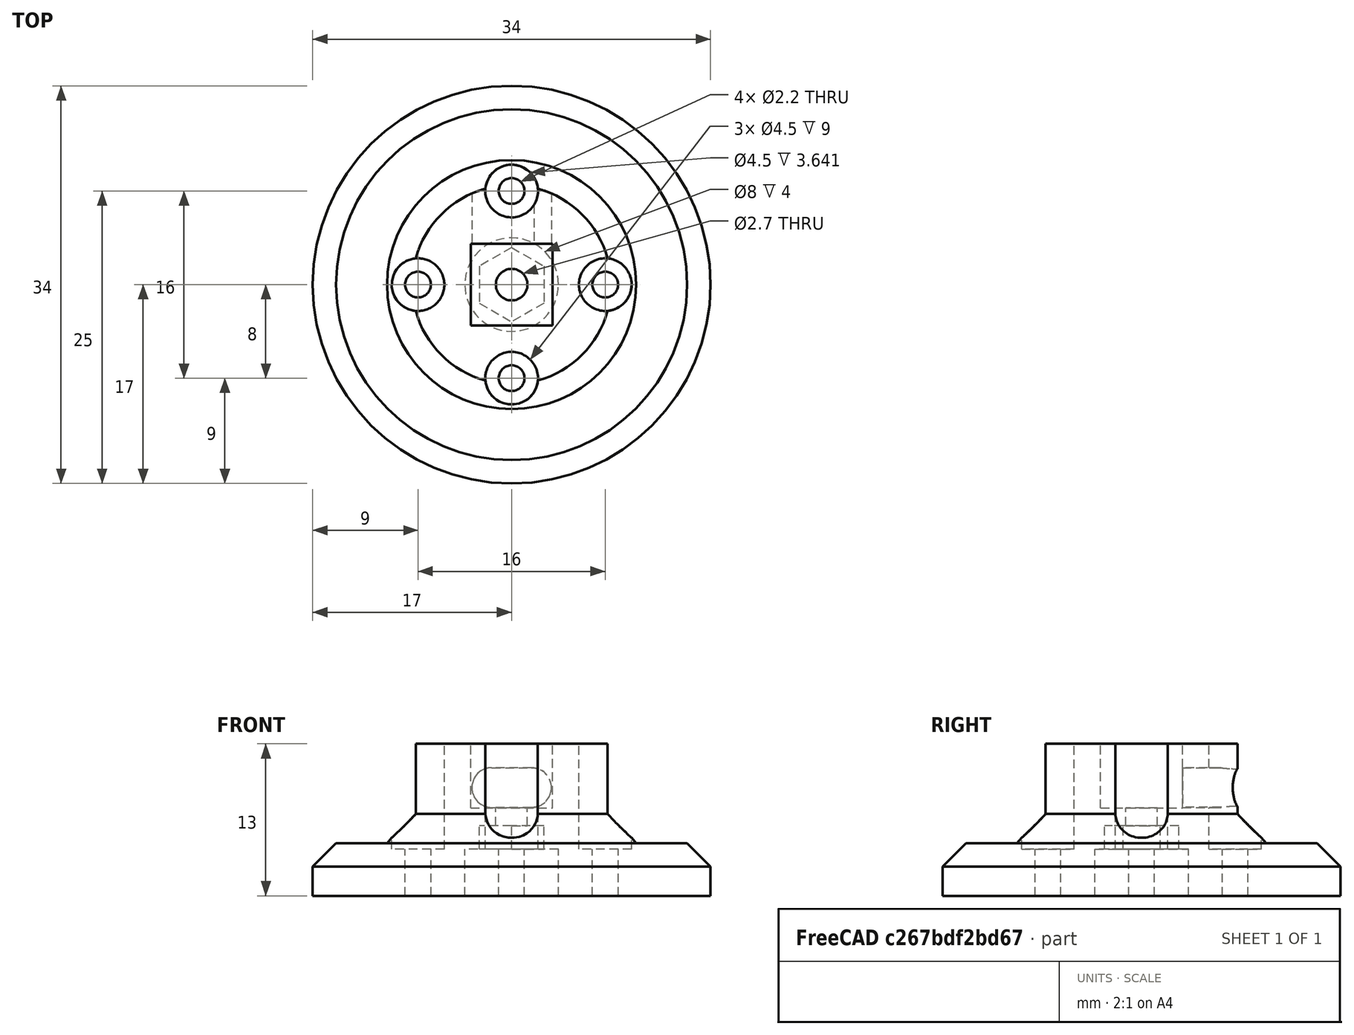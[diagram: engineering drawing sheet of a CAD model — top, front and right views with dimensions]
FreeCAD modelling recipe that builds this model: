
FCSTD DOCUMENT  (FreeCAD 0.14R2935 (Git))
Label: tendon_wheel_ax_9_17_mm
License: CC-BY 3.0
LicenseURL: http://creativecommons.org/licenses/by/3.0/
objects: Part::Cylinder×14, Part::MultiFuse×6, Part::Box×2, Part::Cone×1, Part::Extrusion×1, Part::Mirroring×1, Part::Cut×1, Part::Chamfer×1
note: 27 computed .brp shape members not serialized (recipe doc carries the construction recipe); baked Part::Feature solids carry a one-line shape summary decoded from their .brp

FEATURE [Part::Cylinder] Cylinder
  Angle = 360
  Height = 4.5
  Placement = pos=(0,0,0.5) rot=(0,0,1;0rad)
  Radius = 17
FEATURE [Part::Cone] Cone
  Angle = 360
  Height = 3.5
  Placement = pos=(0,0,4) rot=(0,0,1;0rad)
  Radius1 = 11.5
  Radius2 = 8.5
FEATURE [Part::Cylinder] Cylinder001
  Angle = 360
  Height = 6.5
  Placement = pos=(0,0,7) rot=(0,0,1;0rad)
  Radius = 8.5
FEATURE [Part::Cylinder] Cylinder003  label="TopHole003"
  Angle = 360
  Height = 20
  Placement = pos=(-8,0,-3) rot=(0,0,1;0rad)
  Radius = 1.1
FEATURE [Part::Cylinder] Cylinder004  label="TopHole002"
  Angle = 360
  Height = 20
  Placement = pos=(0,-8,-3) rot=(0,0,1;0rad)
  Radius = 1.1
FEATURE [Part::Cylinder] Cylinder005  label="TopHole001"
  Angle = 360
  Height = 20
  Placement = pos=(8,0,-3) rot=(0,0,1;0rad)
  Radius = 1.1
FEATURE [Part::Cylinder] Cylinder006  label="TopHole"
  Angle = 360
  Height = 10
  Placement = pos=(0,8,-3) rot=(0,0,1;0rad)
  Radius = 1.1
FEATURE [Part::Cylinder] Cylinder007  label="TopHole004"
  Angle = 360
  Height = 20
  Placement = pos=(-8,0,3.5) rot=(0,0,1;0rad)
  Radius = 2.25
FEATURE [Part::Cylinder] Cylinder008  label="TopHole005"
  Angle = 360
  Height = 20
  Placement = pos=(8,0,3.5) rot=(0,0,1;0rad)
  Radius = 2.25
FEATURE [Part::Cylinder] Cylinder009  label="TopHole006"
  Angle = 360
  Height = 20
  Placement = pos=(0,8,3.5) rot=(0,0,1;0rad)
  Radius = 2.25
FEATURE [Part::Cylinder] Cylinder010  label="TopHole007"
  Angle = 360
  Height = 20
  Placement = pos=(0,-8,3.5) rot=(0,0,1;0rad)
  Radius = 2.25
FEATURE [Part::MultiFuse] Fusion001
  Placement = pos=(0,0,1) rot=(0,0,1;0rad)
  Shapes = -> [Cylinder010,Cylinder007,Cylinder005,Cylinder003,Cylinder009,Cylinder004,Cylinder008,Cylinder006]
FEATURE [Part::Cylinder] Cylinder012  label="Cylinder003"
  Angle = 360
  Height = 10
  Placement = pos=(-1.7,12,9.75) rot=(1,0,0;1.5708rad)
  Radius = 1.7
FEATURE [Part::Cylinder] Cylinder013  label="Cylinder004"
  Angle = 360
  Height = 20
  Placement = pos=(0,0,-5) rot=(0,0,1;0rad)
  Radius = 1.35
FEATURE [Part::Box] Box  label="Cube"
  Height = 8
  Length = 7
  Placement = pos=(-3.5,-3.5,8) rot=(0,0,1;0rad)
  Width = 7
FEATURE [Part::Extrusion] Extrude
  Dir = (0,0,2)
  Solid = true
FEATURE [Part::Mirroring] Part__Mirroring  label="Extrude (Mirror #1)"
  Base = (0,0,0)
  Normal = (1,0,0)
  Source = -> Extrude
FEATURE [Part::MultiFuse] Fusion002
  Placement = pos=(0,0,4.5) rot=(0,0,1;0rad)
  Shapes = -> [Part__Mirroring,Extrude]
FEATURE [Part::Cylinder] Cylinder014  label="Cylinder005"
  Angle = 360
  Height = 4.5
  Radius = 4
FEATURE [Part::Cylinder] Cylinder015  label="Cylinder006"
  Angle = 360
  Height = 10
  Placement = pos=(1.7,12,9.75) rot=(1,0,0;1.5708rad)
  Radius = 1.7
FEATURE [Part::Box] Box001  label="Cube001"
  Height = 3.4
  Length = 3.6
  Placement = pos=(-1.7,2,8.05) rot=(0,0,1;0rad)
  Width = 10
FEATURE [Part::MultiFuse] Fusion
  Shapes = -> [Cylinder,Cone,Cylinder001]
FEATURE [Part::MultiFuse] Fusion005
  Shapes = -> [Cylinder014,Fusion002,Cylinder013,Fusion001]
FEATURE [Part::MultiFuse] Fusion006
  Shapes = -> [Cylinder015,Box001,Cylinder012,Box]
FEATURE [Part::MultiFuse] Fusion007
  Shapes = -> [Fusion006,Fusion005]
FEATURE [Part::Cut] Cut
  Base = -> Fusion
  Tool = -> Fusion007
FEATURE [Part::Chamfer] Chamfer
  Base = -> Cut
  Edges = 1 edges r=2: [Edge93]
